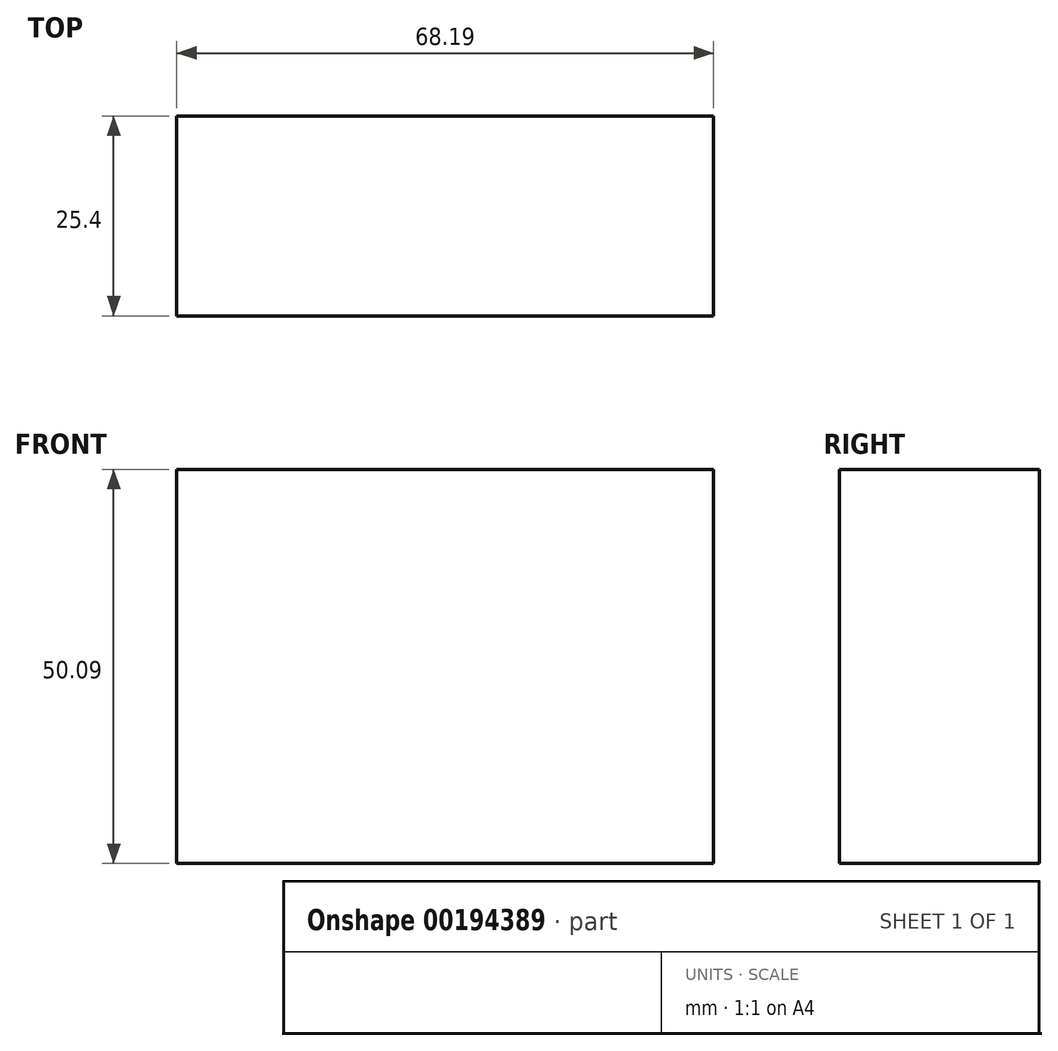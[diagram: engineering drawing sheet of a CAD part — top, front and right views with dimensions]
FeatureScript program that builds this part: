
annotation { "Feature Type Name" : "Feature", "Feature Type Description" : "" }
export const myFeature = defineFeature(function(context is Context, id is Id, definition is map)
    precondition{}
    {
        {
            var Q0;
            Q0=qCreatedBy(makeId("Front.planeOp"),FACE);
            var sketch = newSketch(context, id + "F0", { "sketchPlane" : qUnion([Q0])});
            skLineSegment(sketch, "E0.bottom", {"start": v(0, 0) * mm, "end": v(68.2, 0) * mm});
            skLineSegment(sketch, "E0.top", {"start": v(0, 50.09) * mm, "end": v(68.2, 50.09) * mm});
            skLineSegment(sketch, "E0.left", {"start": v(0, 0) * mm, "end": v(0, 50.09) * mm});
            skLineSegment(sketch, "E0.right", {"start": v(68.2, 0) * mm, "end": v(68.2, 50.09) * mm});
            skSolve(sketch);
        }
        {
            var Q0;
            Q0=makeQuery(id+"F0.imprint","IMPRINT",FACE,{"disambiguationData":[TD([[makeQuery(id+"F0.imprint","IMPRINT",EDGE,{"derivedFrom":sQuery(id+"F0.wireOp",EDGE,"E0.bottom")}),1.0]])]});
            extrude(context, id + "F1", {"entities" : qUnion([Q0]), "depth" : 25.4 * mm});
        }
    });
